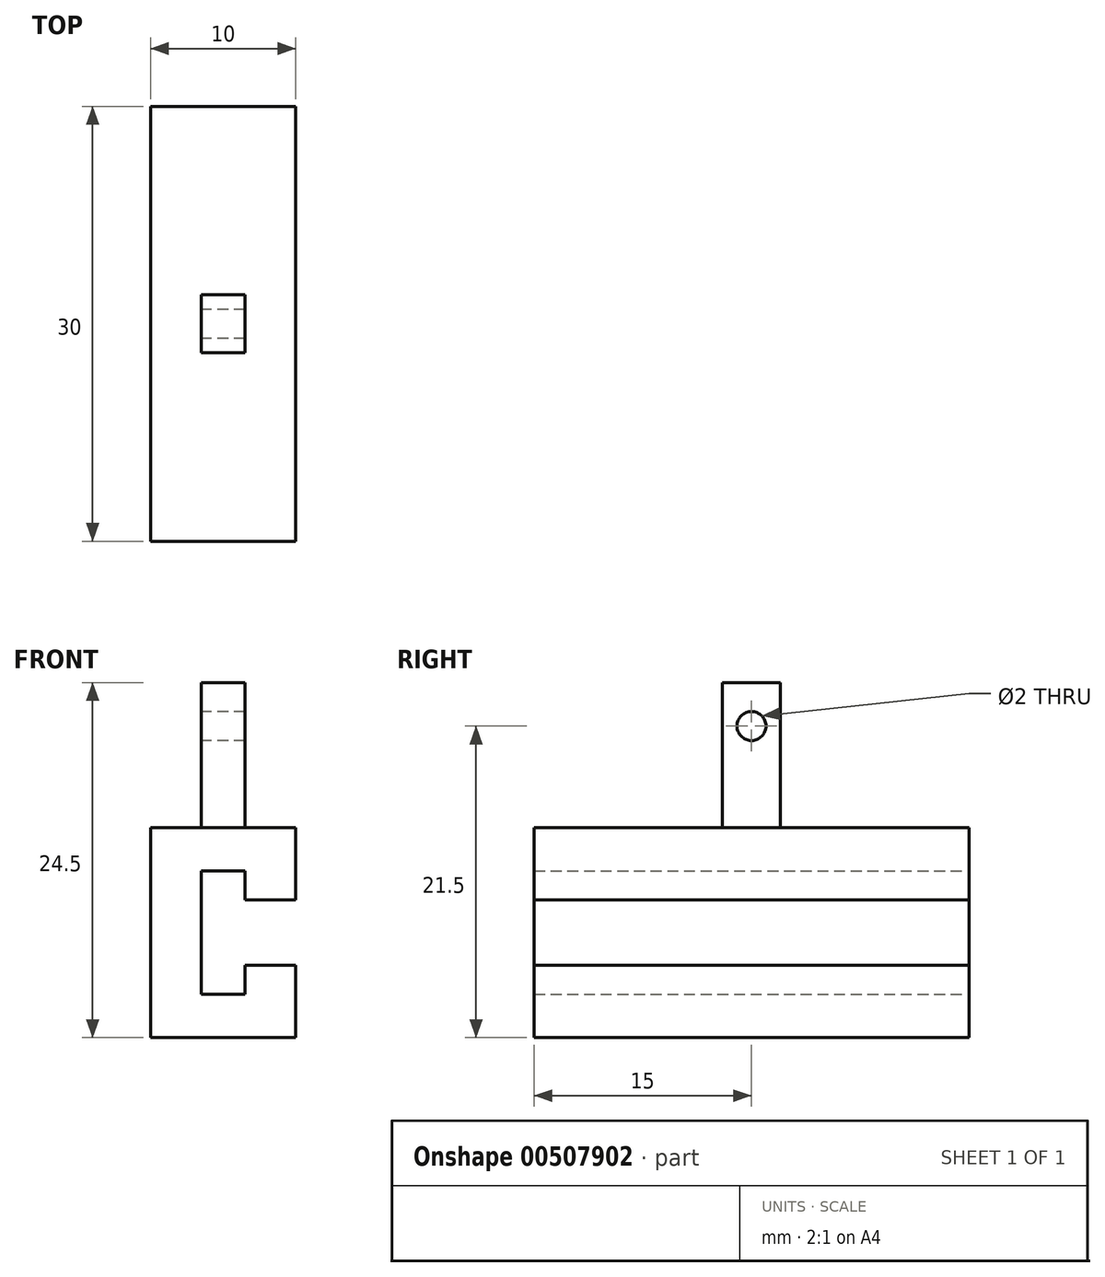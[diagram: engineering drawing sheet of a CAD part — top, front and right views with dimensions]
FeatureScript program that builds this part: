
annotation { "Feature Type Name" : "Feature", "Feature Type Description" : "" }
export const myFeature = defineFeature(function(context is Context, id is Id, definition is map)
    precondition{}
    {
        {
            var Q0;
            Q0=qCreatedBy(makeId("Front.planeOp"),FACE);
            var sketch = newSketch(context, id + "F0", { "sketchPlane" : qUnion([Q0])});
            skLineSegment(sketch, "E0", {"start": v(-13.54, 0) * mm, "end": v(13.96, 0) * mm, "construction": true});
            skLineSegment(sketch, "E1", {"start": v(0, 0) * mm, "end": v(0, 7.25) * mm});
            skLineSegment(sketch, "E2", {"start": v(0, 7.25) * mm, "end": v(10, 7.25) * mm});
            skLineSegment(sketch, "E3", {"start": v(10, 7.25) * mm, "end": v(10, 2.25) * mm});
            skLineSegment(sketch, "E4", {"start": v(10, 2.25) * mm, "end": v(6.5, 2.25) * mm});
            skLineSegment(sketch, "E5", {"start": v(6.5, 2.25) * mm, "end": v(6.5, 4.25) * mm});
            skLineSegment(sketch, "E6", {"start": v(6.5, 4.25) * mm, "end": v(3.5, 4.25) * mm});
            skLineSegment(sketch, "E7", {"start": v(3.5, 4.25) * mm, "end": v(3.5, 0) * mm});
            skLineSegment(sketch, "E8.MirrorCS", {"start": v(0, 0) * mm, "end": v(0, -7.25) * mm});
            skLineSegment(sketch, "E9.MirrorCS", {"start": v(0, -7.25) * mm, "end": v(10, -7.25) * mm});
            skLineSegment(sketch, "E10.MirrorCS", {"start": v(10, -7.25) * mm, "end": v(10, -2.25) * mm});
            skLineSegment(sketch, "E11.MirrorCS", {"start": v(10, -2.25) * mm, "end": v(6.5, -2.25) * mm});
            skLineSegment(sketch, "E12.MirrorCS", {"start": v(6.5, -2.25) * mm, "end": v(6.5, -4.25) * mm});
            skLineSegment(sketch, "E13.MirrorCS", {"start": v(6.5, -4.25) * mm, "end": v(3.5, -4.25) * mm});
            skLineSegment(sketch, "E14.MirrorCS", {"start": v(3.5, -4.25) * mm, "end": v(3.5, 0) * mm});
            skSolve(sketch);
        }
        {
            var Q0;
            Q0=makeQuery(id+"F0.imprint","IMPRINT",FACE,{"disambiguationData":[TD([[makeQuery(id+"F0.imprint","IMPRINT",EDGE,{"derivedFrom":sQuery(id+"F0.wireOp",EDGE,"E1")}),-1.0]])]});
            extrude(context, id + "F1", {"entities" : qUnion([Q0]), "depth" : 30 * mm, "offsetDistance" : 25 * mm});
        }
        {
            var Q0;
            Q0=makeQuery(id+"F1.opExtrude","SWEPT_FACE",FACE,{"disambiguationData":[OSD([sQuery(id+"F0.wireOp",EDGE,"E2")])]});
            var sketch = newSketch(context, id + "F2", { "sketchPlane" : qUnion([Q0])});
            skLineSegment(sketch, "E15", {"start": v(0, -15) * mm, "end": v(10, -15) * mm, "construction": true});
            skLineSegment(sketch, "E16", {"start": v(5, -15) * mm, "end": v(5, -13) * mm, "construction": true});
            skLineSegment(sketch, "E17", {"start": v(5, -13) * mm, "end": v(6.5, -13) * mm});
            skLineSegment(sketch, "E18", {"start": v(6.5, -13) * mm, "end": v(6.5, -15) * mm});
            skLineSegment(sketch, "E19.MirrorCS", {"start": v(5, -13) * mm, "end": v(3.5, -13) * mm});
            skLineSegment(sketch, "E20.MirrorCS", {"start": v(3.5, -13) * mm, "end": v(3.5, -15) * mm});
            skLineSegment(sketch, "E21.MirrorCS", {"start": v(3.5, -17) * mm, "end": v(3.5, -15) * mm});
            skLineSegment(sketch, "E22.MirrorCS", {"start": v(5, -17) * mm, "end": v(3.5, -17) * mm});
            skLineSegment(sketch, "E23.MirrorCS", {"start": v(5, -17) * mm, "end": v(6.5, -17) * mm});
            skLineSegment(sketch, "E24.MirrorCS", {"start": v(6.5, -17) * mm, "end": v(6.5, -15) * mm});
            skSolve(sketch);
        }
        {
            var Q0;
            Q0=makeQuery(id+"F2.imprint","IMPRINT",FACE,{"disambiguationData":[TD([[makeQuery(id+"F2.imprint","IMPRINT",EDGE,{"derivedFrom":sQuery(id+"F2.wireOp",EDGE,"E17")}),-1.0]])]});
            extrude(context, id + "F3", {"entities" : qUnion([Q0]), "operationType" : NewBodyOperationType.ADD, "depth" : 10 * mm, "offsetDistance" : 25 * mm});
        }
        {
            var Q0;
            Q0=makeQuery(id+"F3.opExtrude","SWEPT_FACE",FACE,{"disambiguationData":[OSD([sQuery(id+"F2.wireOp",EDGE,"E20.MirrorCS"),sQuery(id+"F2.wireOp",EDGE,"E21.MirrorCS")])]});
            var sketch = newSketch(context, id + "F4", { "sketchPlane" : qUnion([Q0])});
            skCircle(sketch, "E25", {"center": v(15, 14.25) * mm, "radius": 1 * mm});
            skPoint(sketch, "E25.centerSnap0", {"position": v(15, 17.25) * mm});
            skLineSegment(sketch, "E26", {"start": v(15, 17.25) * mm, "end": v(15, 14.25) * mm, "construction": true});
            skSolve(sketch);
        }
        {
            var Q0;
            Q0 = qSketchRegion(id + "F4", true);
            extrude(context, id + "F5", {"entities" : qUnion([Q0]), "operationType" : NewBodyOperationType.REMOVE, "oppositeDirection" : true, "depth" : 5 * mm, "offsetDistance" : 25 * mm});
        }
    });
